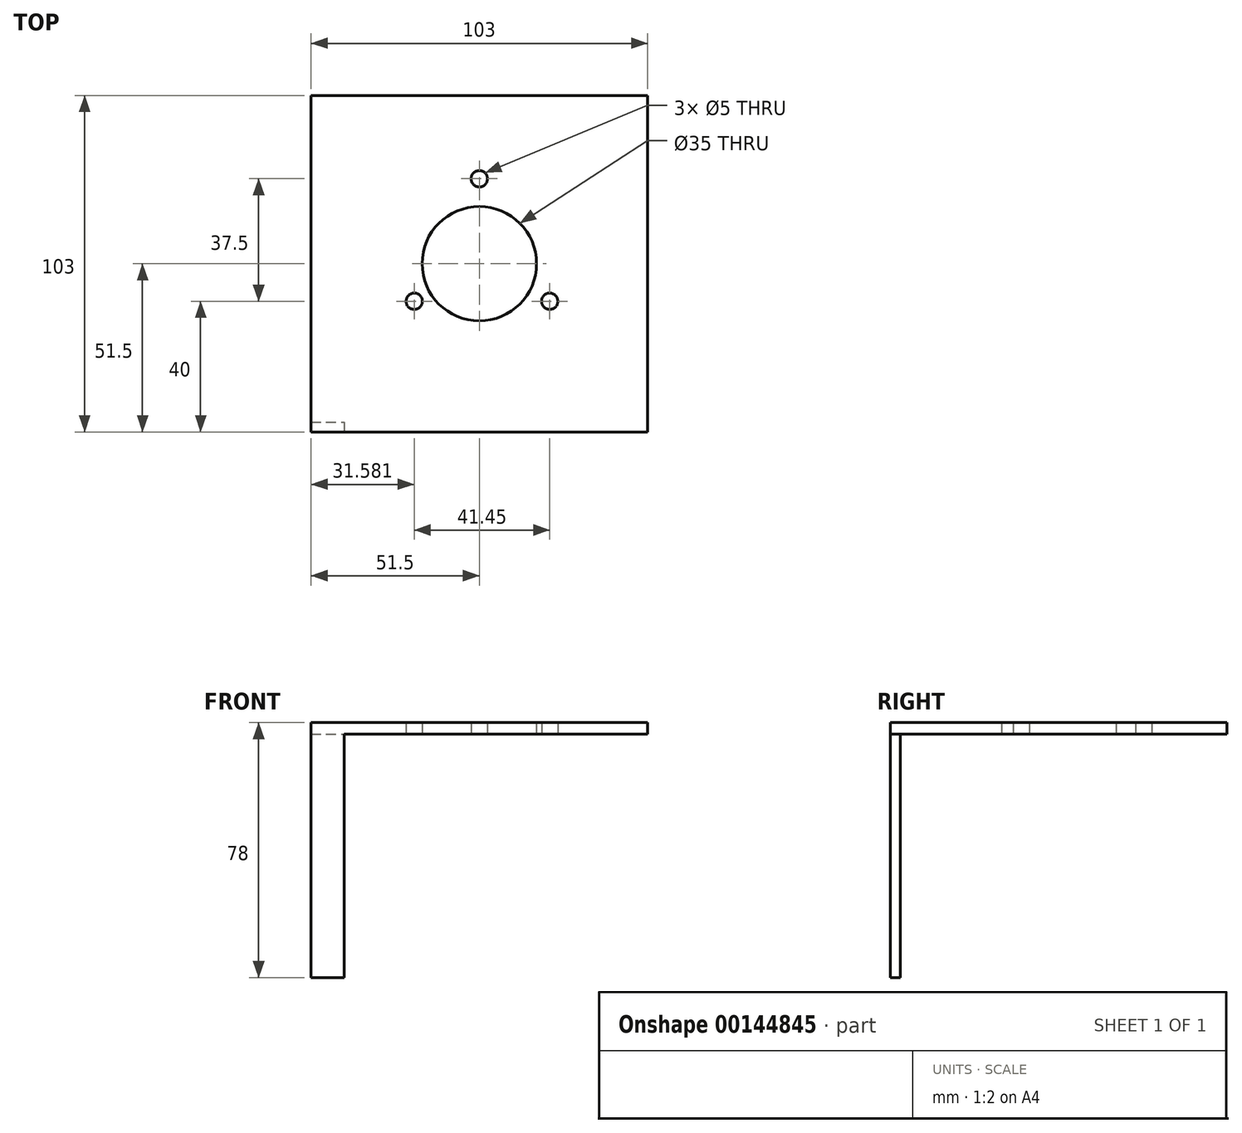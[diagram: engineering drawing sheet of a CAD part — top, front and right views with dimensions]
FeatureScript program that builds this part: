
annotation { "Feature Type Name" : "Feature", "Feature Type Description" : "" }
export const myFeature = defineFeature(function(context is Context, id is Id, definition is map)
    precondition{}
    {
        {
            var Q0;
            Q0=qCreatedBy(makeId("Top.planeOp"),FACE);
            var sketch = newSketch(context, id + "F0", { "sketchPlane" : qUnion([Q0])});
            skCircle(sketch, "E0", {"center": v(0, 0) * mm, "radius": 17.5 * mm});
            skLineSegment(sketch, "E1.bottom", {"start": v(-51.5, 51.5) * mm, "end": v(51.5, 51.5) * mm});
            skLineSegment(sketch, "E1.top", {"start": v(-51.5, -51.5) * mm, "end": v(51.5, -51.5) * mm});
            skLineSegment(sketch, "E1.left", {"start": v(-51.5, 51.5) * mm, "end": v(-51.5, -51.5) * mm});
            skLineSegment(sketch, "E1.right", {"start": v(51.5, 51.5) * mm, "end": v(51.5, -51.5) * mm});
            skCircle(sketch, "E2", {"center": v(0, 26) * mm, "radius": 2.5 * mm});
            skLineSegment(sketch, "E3", {"start": v(0, 26) * mm, "end": v(0, 0) * mm, "construction": true});
            skLineSegment(sketch, "E4", {"start": v(0, 0) * mm, "end": v(-19.92, -11.5) * mm, "construction": true});
            skLineSegment(sketch, "E5", {"start": v(1.61, 0) * mm, "end": v(21.53, -11.5) * mm, "construction": true});
            skCircle(sketch, "E6", {"center": v(-19.92, -11.5) * mm, "radius": 2.5 * mm});
            skCircle(sketch, "E7", {"center": v(21.53, -11.5) * mm, "radius": 2.5 * mm});
            skSolve(sketch);
        }
        {
            var Q0;
            Q0 = qSketchRegion(id + "F0", true);
            extrude(context, id + "F1", {"entities" : qUnion([Q0]), "depth" : 3.5 * mm});
        }
        {
            var Q0;
            Q0=makeQuery(id+"F1.opExtrude","SWEPT_FACE",FACE,{"disambiguationData":[OSD([sQuery(id+"F0.wireOp",EDGE,"E1.top")])]});
            var sketch = newSketch(context, id + "F2", { "sketchPlane" : qUnion([Q0])});
            skLineSegment(sketch, "E8.bottom", {"start": v(-51.5, 0) * mm, "end": v(-41.3, 0) * mm});
            skLineSegment(sketch, "E8.top", {"start": v(-51.5, -74.5) * mm, "end": v(-41.3, -74.5) * mm});
            skLineSegment(sketch, "E8.left", {"start": v(-51.5, 0) * mm, "end": v(-51.5, -74.5) * mm});
            skLineSegment(sketch, "E8.right", {"start": v(-41.3, 0) * mm, "end": v(-41.3, -74.5) * mm});
            skSolve(sketch);
        }
        {
            var Q0;
            Q0=makeQuery(id+"F2.imprint","IMPRINT",FACE,{"disambiguationData":[TD([[makeQuery(id+"F2.imprint","IMPRINT",EDGE,{"derivedFrom":sQuery(id+"F2.wireOp",EDGE,"E8.bottom")}),-1.0]])]});
            extrude(context, id + "F3", {"entities" : qUnion([Q0]), "operationType" : NewBodyOperationType.ADD, "oppositeDirection" : true, "depth" : 3 * mm});
        }
    });
